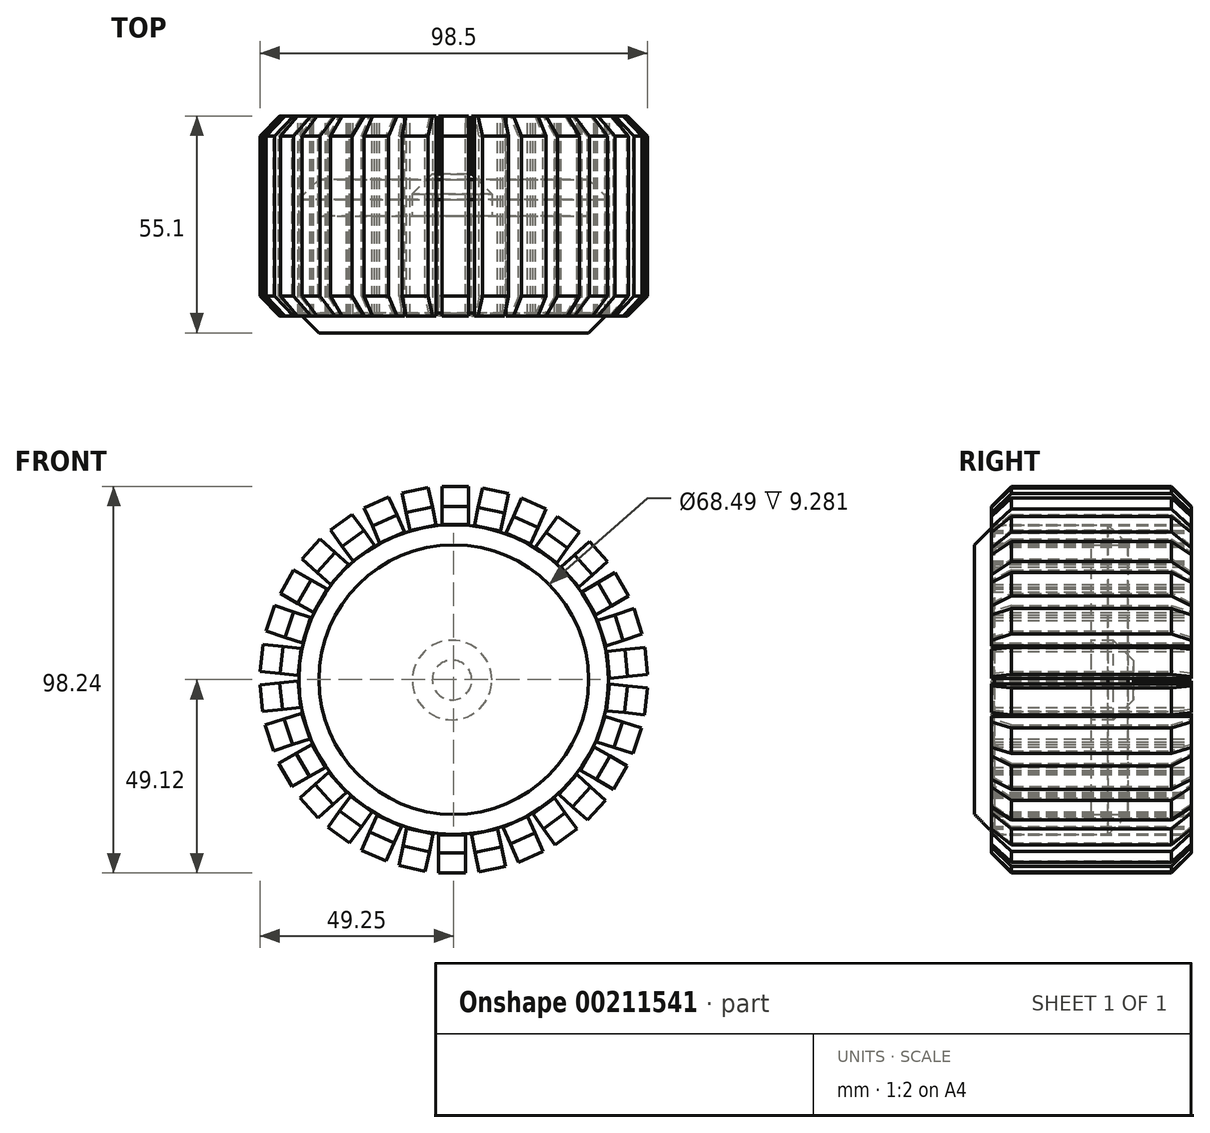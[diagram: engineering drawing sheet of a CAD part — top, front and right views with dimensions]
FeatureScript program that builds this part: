
annotation { "Feature Type Name" : "Feature", "Feature Type Description" : "" }
export const myFeature = defineFeature(function(context is Context, id is Id, definition is map)
    precondition{}
    {
        {
            var Q0;
            Q0=qCreatedBy(makeId("Front.planeOp"),FACE);
            var sketch = newSketch(context, id + "F0", { "sketchPlane" : qUnion([Q0])});
            skCircle(sketch, "E0", {"center": v(0, 0) * mm, "radius": 39.32 * mm});
            skSolve(sketch);
        }
        {
            var Q0;
            Q0 = qSketchRegion(id + "F0", true);
            extrude(context, id + "F1", {"entities" : qUnion([Q0]), "depth" : 38.98 * mm});
        }
        {
            var Q0;
            Q0=makeQuery(id+"F1.opExtrude","SWEPT_FACE",FACE,{"disambiguationData":[OSD([sQuery(id+"F0.wireOp",EDGE,"E0")])]});
            chamfer(context, id + "F9", {"entities" : qUnion([Q0]), "width" : 5.08 * mm, "tangentPropagation" : true});
        }
        {
            var Q0;
            Q0=makeQuery(id+"F1.opExtrude","CAP_FACE",FACE,{"disambiguationData":[OSD([sQuery(id+"F0.wireOp",EDGE,"E0")])],"isStart":false});
            var sketch = newSketch(context, id + "F10", { "sketchPlane" : qUnion([Q0])});
            skCircle(sketch, "E1", {"center": v(-0.43, -0.11) * mm, "radius": 10.1 * mm});
            skSolve(sketch);
        }
        {
            var Q0;
            Q0=makeQuery(id+"F10.imprint","IMPRINT",FACE,{"disambiguationData":[TD([[makeQuery(id+"F10.imprint","IMPRINT",EDGE,{"derivedFrom":sQuery(id+"F10.wireOp",EDGE,"E1")}),1.0]])]});
            extrude(context, id + "F2", {"entities" : qUnion([Q0]), "operationType" : NewBodyOperationType.ADD, "oppositeDirection" : true, "depth" : 40.36 * mm});
        }
        {
            var Q0;
            Q0=makeQuery(id+"F1.opExtrude","CAP_FACE",FACE,{"disambiguationData":[OSD([sQuery(id+"F0.wireOp",EDGE,"E0")])],"isStart":true});
            extrude(context, id + "F3", {"entities" : qUnion([Q0]), "operationType" : NewBodyOperationType.REMOVE, "oppositeDirection" : true, "depth" : 9.28 * mm});
        }
        {
            var Q0;
            Q0=makeQuery(id+"F2.opExtrude","CAP_EDGE",EDGE,{"disambiguationData":[OSD([sQuery(id+"F10.wireOp",EDGE,"E1")])],"isStart":false});
            chamfer(context, id + "F4", {"entities" : qUnion([Q0]), "width" : 5.08 * mm, "tangentPropagation" : true});
        }
        {
            var Q0;
            Q0=makeQuery(id+"F3.boolean.opBoolean","COPY",FACE,{"derivedFrom":makeQuery(id+"F3.opExtrude","CAP_FACE",FACE,{"disambiguationData":[OSD([sQuery(id+"F0.wireOp",EDGE,"E0")])],"isStart":false})});
            cPlane(context, id + "F5", {"entities" : qUnion([Q0]), "cplaneType" : CPlaneType.OFFSET, "offset" : 25.4 * mm, "width" : 152.4 * mm, "height" : 152.4 * mm});
        }
        {
            var Q0;
            Q0=qCreatedBy(id+"F5.planeOp",FACE);
            var sketch = newSketch(context, id + "F6", { "sketchPlane" : qUnion([Q0])});
            skLineSegment(sketch, "E2.bottom", {"start": v(3.02, 39.41) * mm, "end": v(-3.8, 39.41) * mm});
            skLineSegment(sketch, "E2.top", {"start": v(3.02, 49.12) * mm, "end": v(-3.8, 49.12) * mm});
            skLineSegment(sketch, "E2.left", {"start": v(3.02, 39.41) * mm, "end": v(3.02, 49.12) * mm});
            skLineSegment(sketch, "E2.right", {"start": v(-3.8, 39.41) * mm, "end": v(-3.8, 49.12) * mm});
            skPoint(sketch, "E2.middle", {"position": v(-0.4, 44.27) * mm});
            skSolve(sketch);
        }
        {
            var Q0;
            Q0 = qSketchRegion(id + "F6", true);
            extrude(context, id + "F11", {"entities" : qUnion([Q0]), "oppositeDirection" : true, "depth" : 50.8 * mm});
        }
        {
            var Q0;
            Q0=makeQuery(id+"F11.opExtrude","SWEPT_BODY",BODY,{"disambiguationData":[OSD([sQuery(id+"F6.wireOp",EDGE,"E2.bottom"),sQuery(id+"F6.wireOp",EDGE,"E2.top"),sQuery(id+"F6.wireOp",EDGE,"E2.left"),sQuery(id+"F6.wireOp",EDGE,"E2.right")])]});
            var Q1;
            Q1=makeQuery(id+"F1.opExtrude","SWEPT_FACE",FACE,{"disambiguationData":[OSD([sQuery(id+"F0.wireOp",EDGE,"E0")])]});
            circularPattern(context, id + "F7", {"operationType" : NewBodyOperationType.ADD, "entities" : qUnion([Q0]), "axis" : qUnion([Q1]), "angle" : 360 * degree, "instanceCount" : 30, "equalSpace" : true});
        }
        {
            var Q0;
            Q0=makeQuery(id+"F7.opPattern","COPY",EDGE,{"derivedFrom":makeQuery(id+"F11.opExtrude","CAP_EDGE",EDGE,{"disambiguationData":[OSD([sQuery(id+"F6.wireOp",EDGE,"E2.top")])],"isStart":false}),"instanceName":"29"});
            var Q1;
            Q1=makeQuery(id+"F11.opExtrude","CAP_EDGE",EDGE,{"disambiguationData":[OSD([sQuery(id+"F6.wireOp",EDGE,"E2.top")])],"isStart":false});
            var Q2;
            Q2=makeQuery(id+"F7.opPattern","COPY",EDGE,{"derivedFrom":makeQuery(id+"F11.opExtrude","CAP_EDGE",EDGE,{"disambiguationData":[OSD([sQuery(id+"F6.wireOp",EDGE,"E2.top")])],"isStart":false}),"instanceName":"1"});
            var Q3;
            Q3=makeQuery(id+"F7.opPattern","COPY",EDGE,{"derivedFrom":makeQuery(id+"F11.opExtrude","CAP_EDGE",EDGE,{"disambiguationData":[OSD([sQuery(id+"F6.wireOp",EDGE,"E2.top")])],"isStart":false}),"instanceName":"2"});
            var Q4;
            Q4=makeQuery(id+"F7.opPattern","COPY",EDGE,{"derivedFrom":makeQuery(id+"F11.opExtrude","CAP_EDGE",EDGE,{"disambiguationData":[OSD([sQuery(id+"F6.wireOp",EDGE,"E2.top")])],"isStart":false}),"instanceName":"3"});
            var Q5;
            Q5=makeQuery(id+"F7.opPattern","COPY",EDGE,{"derivedFrom":makeQuery(id+"F11.opExtrude","CAP_EDGE",EDGE,{"disambiguationData":[OSD([sQuery(id+"F6.wireOp",EDGE,"E2.top")])],"isStart":false}),"instanceName":"4"});
            var Q6;
            Q6=makeQuery(id+"F7.opPattern","COPY",EDGE,{"derivedFrom":makeQuery(id+"F11.opExtrude","CAP_EDGE",EDGE,{"disambiguationData":[OSD([sQuery(id+"F6.wireOp",EDGE,"E2.top")])],"isStart":false}),"instanceName":"5"});
            var Q7;
            Q7=makeQuery(id+"F7.opPattern","COPY",EDGE,{"derivedFrom":makeQuery(id+"F11.opExtrude","CAP_EDGE",EDGE,{"disambiguationData":[OSD([sQuery(id+"F6.wireOp",EDGE,"E2.top")])],"isStart":false}),"instanceName":"6"});
            var Q8;
            Q8=makeQuery(id+"F7.opPattern","COPY",EDGE,{"derivedFrom":makeQuery(id+"F11.opExtrude","CAP_EDGE",EDGE,{"disambiguationData":[OSD([sQuery(id+"F6.wireOp",EDGE,"E2.top")])],"isStart":false}),"instanceName":"7"});
            var Q9;
            Q9=makeQuery(id+"F7.opPattern","COPY",EDGE,{"derivedFrom":makeQuery(id+"F11.opExtrude","CAP_EDGE",EDGE,{"disambiguationData":[OSD([sQuery(id+"F6.wireOp",EDGE,"E2.top")])],"isStart":false}),"instanceName":"8"});
            var Q10;
            Q10=makeQuery(id+"F7.opPattern","COPY",EDGE,{"derivedFrom":makeQuery(id+"F11.opExtrude","CAP_EDGE",EDGE,{"disambiguationData":[OSD([sQuery(id+"F6.wireOp",EDGE,"E2.top")])],"isStart":false}),"instanceName":"9"});
            var Q11;
            Q11=makeQuery(id+"F7.opPattern","COPY",EDGE,{"derivedFrom":makeQuery(id+"F11.opExtrude","CAP_EDGE",EDGE,{"disambiguationData":[OSD([sQuery(id+"F6.wireOp",EDGE,"E2.top")])],"isStart":false}),"instanceName":"10"});
            var Q12;
            Q12=makeQuery(id+"F7.opPattern","COPY",EDGE,{"derivedFrom":makeQuery(id+"F11.opExtrude","CAP_EDGE",EDGE,{"disambiguationData":[OSD([sQuery(id+"F6.wireOp",EDGE,"E2.top")])],"isStart":false}),"instanceName":"11"});
            var Q13;
            Q13=makeQuery(id+"F7.opPattern","COPY",EDGE,{"derivedFrom":makeQuery(id+"F11.opExtrude","CAP_EDGE",EDGE,{"disambiguationData":[OSD([sQuery(id+"F6.wireOp",EDGE,"E2.top")])],"isStart":false}),"instanceName":"12"});
            var Q14;
            Q14=makeQuery(id+"F7.opPattern","COPY",EDGE,{"derivedFrom":makeQuery(id+"F11.opExtrude","CAP_EDGE",EDGE,{"disambiguationData":[OSD([sQuery(id+"F6.wireOp",EDGE,"E2.top")])],"isStart":false}),"instanceName":"13"});
            var Q15;
            Q15=makeQuery(id+"F7.opPattern","COPY",EDGE,{"derivedFrom":makeQuery(id+"F11.opExtrude","CAP_EDGE",EDGE,{"disambiguationData":[OSD([sQuery(id+"F6.wireOp",EDGE,"E2.top")])],"isStart":false}),"instanceName":"14"});
            var Q16;
            Q16=makeQuery(id+"F7.opPattern","COPY",EDGE,{"derivedFrom":makeQuery(id+"F11.opExtrude","CAP_EDGE",EDGE,{"disambiguationData":[OSD([sQuery(id+"F6.wireOp",EDGE,"E2.top")])],"isStart":false}),"instanceName":"15"});
            var Q17;
            Q17=makeQuery(id+"F7.opPattern","COPY",EDGE,{"derivedFrom":makeQuery(id+"F11.opExtrude","CAP_EDGE",EDGE,{"disambiguationData":[OSD([sQuery(id+"F6.wireOp",EDGE,"E2.top")])],"isStart":false}),"instanceName":"16"});
            var Q18;
            Q18=makeQuery(id+"F7.opPattern","COPY",EDGE,{"derivedFrom":makeQuery(id+"F11.opExtrude","CAP_EDGE",EDGE,{"disambiguationData":[OSD([sQuery(id+"F6.wireOp",EDGE,"E2.top")])],"isStart":false}),"instanceName":"17"});
            var Q19;
            Q19=makeQuery(id+"F7.opPattern","COPY",EDGE,{"derivedFrom":makeQuery(id+"F11.opExtrude","CAP_EDGE",EDGE,{"disambiguationData":[OSD([sQuery(id+"F6.wireOp",EDGE,"E2.top")])],"isStart":false}),"instanceName":"18"});
            var Q20;
            Q20=makeQuery(id+"F7.opPattern","COPY",EDGE,{"derivedFrom":makeQuery(id+"F11.opExtrude","CAP_EDGE",EDGE,{"disambiguationData":[OSD([sQuery(id+"F6.wireOp",EDGE,"E2.top")])],"isStart":false}),"instanceName":"19"});
            var Q21;
            Q21=makeQuery(id+"F7.opPattern","COPY",EDGE,{"derivedFrom":makeQuery(id+"F11.opExtrude","CAP_EDGE",EDGE,{"disambiguationData":[OSD([sQuery(id+"F6.wireOp",EDGE,"E2.top")])],"isStart":false}),"instanceName":"20"});
            var Q22;
            Q22=makeQuery(id+"F7.opPattern","COPY",EDGE,{"derivedFrom":makeQuery(id+"F11.opExtrude","CAP_EDGE",EDGE,{"disambiguationData":[OSD([sQuery(id+"F6.wireOp",EDGE,"E2.top")])],"isStart":false}),"instanceName":"21"});
            var Q23;
            Q23=makeQuery(id+"F7.opPattern","COPY",EDGE,{"derivedFrom":makeQuery(id+"F11.opExtrude","CAP_EDGE",EDGE,{"disambiguationData":[OSD([sQuery(id+"F6.wireOp",EDGE,"E2.top")])],"isStart":false}),"instanceName":"22"});
            var Q24;
            Q24=makeQuery(id+"F7.opPattern","COPY",EDGE,{"derivedFrom":makeQuery(id+"F11.opExtrude","CAP_EDGE",EDGE,{"disambiguationData":[OSD([sQuery(id+"F6.wireOp",EDGE,"E2.top")])],"isStart":false}),"instanceName":"23"});
            var Q25;
            Q25=makeQuery(id+"F7.opPattern","COPY",EDGE,{"derivedFrom":makeQuery(id+"F11.opExtrude","CAP_EDGE",EDGE,{"disambiguationData":[OSD([sQuery(id+"F6.wireOp",EDGE,"E2.top")])],"isStart":false}),"instanceName":"24"});
            var Q26;
            Q26=makeQuery(id+"F7.opPattern","COPY",EDGE,{"derivedFrom":makeQuery(id+"F11.opExtrude","CAP_EDGE",EDGE,{"disambiguationData":[OSD([sQuery(id+"F6.wireOp",EDGE,"E2.top")])],"isStart":false}),"instanceName":"25"});
            var Q27;
            Q27=makeQuery(id+"F7.opPattern","COPY",EDGE,{"derivedFrom":makeQuery(id+"F11.opExtrude","CAP_EDGE",EDGE,{"disambiguationData":[OSD([sQuery(id+"F6.wireOp",EDGE,"E2.top")])],"isStart":false}),"instanceName":"26"});
            var Q28;
            Q28=makeQuery(id+"F7.opPattern","COPY",EDGE,{"derivedFrom":makeQuery(id+"F11.opExtrude","CAP_EDGE",EDGE,{"disambiguationData":[OSD([sQuery(id+"F6.wireOp",EDGE,"E2.top")])],"isStart":false}),"instanceName":"27"});
            var Q29;
            Q29=makeQuery(id+"F7.opPattern","COPY",EDGE,{"derivedFrom":makeQuery(id+"F11.opExtrude","CAP_EDGE",EDGE,{"disambiguationData":[OSD([sQuery(id+"F6.wireOp",EDGE,"E2.top")])],"isStart":false}),"instanceName":"28"});
            chamfer(context, id + "F12", {"entities" : qUnion([Q0, Q1, Q2, Q3, Q4, Q5, Q6, Q7, Q8, Q9, Q10, Q11, Q12, Q13, Q14, Q15, Q16, Q17, Q18, Q19, Q20, Q21, Q22, Q23, Q24, Q25, Q26, Q27, Q28, Q29]), "width" : 5.08 * mm, "tangentPropagation" : true});
        }
        {
            var Q0;
            Q0=makeQuery(id+"F7.opPattern","COPY",EDGE,{"derivedFrom":makeQuery(id+"F11.opExtrude","CAP_EDGE",EDGE,{"disambiguationData":[OSD([sQuery(id+"F6.wireOp",EDGE,"E2.top")])],"isStart":true}),"instanceName":"28"});
            var Q1;
            Q1=makeQuery(id+"F7.opPattern","COPY",EDGE,{"derivedFrom":makeQuery(id+"F11.opExtrude","CAP_EDGE",EDGE,{"disambiguationData":[OSD([sQuery(id+"F6.wireOp",EDGE,"E2.top")])],"isStart":true}),"instanceName":"27"});
            var Q2;
            Q2=makeQuery(id+"F7.opPattern","COPY",EDGE,{"derivedFrom":makeQuery(id+"F11.opExtrude","CAP_EDGE",EDGE,{"disambiguationData":[OSD([sQuery(id+"F6.wireOp",EDGE,"E2.top")])],"isStart":true}),"instanceName":"29"});
            var Q3;
            Q3=makeQuery(id+"F11.opExtrude","CAP_EDGE",EDGE,{"disambiguationData":[OSD([sQuery(id+"F6.wireOp",EDGE,"E2.top")])],"isStart":true});
            var Q4;
            Q4=makeQuery(id+"F7.opPattern","COPY",EDGE,{"derivedFrom":makeQuery(id+"F11.opExtrude","CAP_EDGE",EDGE,{"disambiguationData":[OSD([sQuery(id+"F6.wireOp",EDGE,"E2.top")])],"isStart":true}),"instanceName":"1"});
            var Q5;
            Q5=makeQuery(id+"F7.opPattern","COPY",EDGE,{"derivedFrom":makeQuery(id+"F11.opExtrude","CAP_EDGE",EDGE,{"disambiguationData":[OSD([sQuery(id+"F6.wireOp",EDGE,"E2.top")])],"isStart":true}),"instanceName":"2"});
            var Q6;
            Q6=makeQuery(id+"F7.opPattern","COPY",EDGE,{"derivedFrom":makeQuery(id+"F11.opExtrude","CAP_EDGE",EDGE,{"disambiguationData":[OSD([sQuery(id+"F6.wireOp",EDGE,"E2.top")])],"isStart":true}),"instanceName":"3"});
            var Q7;
            Q7=makeQuery(id+"F7.opPattern","COPY",EDGE,{"derivedFrom":makeQuery(id+"F11.opExtrude","CAP_EDGE",EDGE,{"disambiguationData":[OSD([sQuery(id+"F6.wireOp",EDGE,"E2.top")])],"isStart":true}),"instanceName":"4"});
            var Q8;
            Q8=makeQuery(id+"F7.opPattern","COPY",EDGE,{"derivedFrom":makeQuery(id+"F11.opExtrude","CAP_EDGE",EDGE,{"disambiguationData":[OSD([sQuery(id+"F6.wireOp",EDGE,"E2.top")])],"isStart":true}),"instanceName":"5"});
            var Q9;
            Q9=makeQuery(id+"F7.opPattern","COPY",EDGE,{"derivedFrom":makeQuery(id+"F11.opExtrude","CAP_EDGE",EDGE,{"disambiguationData":[OSD([sQuery(id+"F6.wireOp",EDGE,"E2.top")])],"isStart":true}),"instanceName":"6"});
            var Q10;
            Q10=makeQuery(id+"F7.opPattern","COPY",EDGE,{"derivedFrom":makeQuery(id+"F11.opExtrude","CAP_EDGE",EDGE,{"disambiguationData":[OSD([sQuery(id+"F6.wireOp",EDGE,"E2.top")])],"isStart":true}),"instanceName":"7"});
            var Q11;
            Q11=makeQuery(id+"F7.opPattern","COPY",EDGE,{"derivedFrom":makeQuery(id+"F11.opExtrude","CAP_EDGE",EDGE,{"disambiguationData":[OSD([sQuery(id+"F6.wireOp",EDGE,"E2.top")])],"isStart":true}),"instanceName":"8"});
            var Q12;
            Q12=makeQuery(id+"F7.opPattern","COPY",EDGE,{"derivedFrom":makeQuery(id+"F11.opExtrude","CAP_EDGE",EDGE,{"disambiguationData":[OSD([sQuery(id+"F6.wireOp",EDGE,"E2.top")])],"isStart":true}),"instanceName":"9"});
            var Q13;
            Q13=makeQuery(id+"F7.opPattern","COPY",EDGE,{"derivedFrom":makeQuery(id+"F11.opExtrude","CAP_EDGE",EDGE,{"disambiguationData":[OSD([sQuery(id+"F6.wireOp",EDGE,"E2.top")])],"isStart":true}),"instanceName":"10"});
            var Q14;
            Q14=makeQuery(id+"F7.opPattern","COPY",EDGE,{"derivedFrom":makeQuery(id+"F11.opExtrude","CAP_EDGE",EDGE,{"disambiguationData":[OSD([sQuery(id+"F6.wireOp",EDGE,"E2.top")])],"isStart":true}),"instanceName":"11"});
            var Q15;
            Q15=makeQuery(id+"F7.opPattern","COPY",EDGE,{"derivedFrom":makeQuery(id+"F11.opExtrude","CAP_EDGE",EDGE,{"disambiguationData":[OSD([sQuery(id+"F6.wireOp",EDGE,"E2.top")])],"isStart":true}),"instanceName":"12"});
            var Q16;
            Q16=makeQuery(id+"F7.opPattern","COPY",EDGE,{"derivedFrom":makeQuery(id+"F11.opExtrude","CAP_EDGE",EDGE,{"disambiguationData":[OSD([sQuery(id+"F6.wireOp",EDGE,"E2.top")])],"isStart":true}),"instanceName":"13"});
            var Q17;
            Q17=makeQuery(id+"F7.opPattern","COPY",EDGE,{"derivedFrom":makeQuery(id+"F11.opExtrude","CAP_EDGE",EDGE,{"disambiguationData":[OSD([sQuery(id+"F6.wireOp",EDGE,"E2.top")])],"isStart":true}),"instanceName":"14"});
            var Q18;
            Q18=makeQuery(id+"F7.opPattern","COPY",EDGE,{"derivedFrom":makeQuery(id+"F11.opExtrude","CAP_EDGE",EDGE,{"disambiguationData":[OSD([sQuery(id+"F6.wireOp",EDGE,"E2.top")])],"isStart":true}),"instanceName":"15"});
            var Q19;
            Q19=makeQuery(id+"F7.opPattern","COPY",EDGE,{"derivedFrom":makeQuery(id+"F11.opExtrude","CAP_EDGE",EDGE,{"disambiguationData":[OSD([sQuery(id+"F6.wireOp",EDGE,"E2.top")])],"isStart":true}),"instanceName":"16"});
            var Q20;
            Q20=makeQuery(id+"F7.opPattern","COPY",EDGE,{"derivedFrom":makeQuery(id+"F11.opExtrude","CAP_EDGE",EDGE,{"disambiguationData":[OSD([sQuery(id+"F6.wireOp",EDGE,"E2.top")])],"isStart":true}),"instanceName":"17"});
            var Q21;
            Q21=makeQuery(id+"F7.opPattern","COPY",EDGE,{"derivedFrom":makeQuery(id+"F11.opExtrude","CAP_EDGE",EDGE,{"disambiguationData":[OSD([sQuery(id+"F6.wireOp",EDGE,"E2.top")])],"isStart":true}),"instanceName":"18"});
            var Q22;
            Q22=makeQuery(id+"F7.opPattern","COPY",EDGE,{"derivedFrom":makeQuery(id+"F11.opExtrude","CAP_EDGE",EDGE,{"disambiguationData":[OSD([sQuery(id+"F6.wireOp",EDGE,"E2.top")])],"isStart":true}),"instanceName":"19"});
            var Q23;
            Q23=makeQuery(id+"F7.opPattern","COPY",EDGE,{"derivedFrom":makeQuery(id+"F11.opExtrude","CAP_EDGE",EDGE,{"disambiguationData":[OSD([sQuery(id+"F6.wireOp",EDGE,"E2.top")])],"isStart":true}),"instanceName":"20"});
            var Q24;
            Q24=makeQuery(id+"F7.opPattern","COPY",EDGE,{"derivedFrom":makeQuery(id+"F11.opExtrude","CAP_EDGE",EDGE,{"disambiguationData":[OSD([sQuery(id+"F6.wireOp",EDGE,"E2.top")])],"isStart":true}),"instanceName":"21"});
            var Q25;
            Q25=makeQuery(id+"F7.opPattern","COPY",EDGE,{"derivedFrom":makeQuery(id+"F11.opExtrude","CAP_EDGE",EDGE,{"disambiguationData":[OSD([sQuery(id+"F6.wireOp",EDGE,"E2.top")])],"isStart":true}),"instanceName":"22"});
            var Q26;
            Q26=makeQuery(id+"F7.opPattern","COPY",EDGE,{"derivedFrom":makeQuery(id+"F11.opExtrude","CAP_EDGE",EDGE,{"disambiguationData":[OSD([sQuery(id+"F6.wireOp",EDGE,"E2.top")])],"isStart":true}),"instanceName":"23"});
            var Q27;
            Q27=makeQuery(id+"F7.opPattern","COPY",EDGE,{"derivedFrom":makeQuery(id+"F11.opExtrude","CAP_EDGE",EDGE,{"disambiguationData":[OSD([sQuery(id+"F6.wireOp",EDGE,"E2.top")])],"isStart":true}),"instanceName":"24"});
            var Q28;
            Q28=makeQuery(id+"F7.opPattern","COPY",EDGE,{"derivedFrom":makeQuery(id+"F11.opExtrude","CAP_EDGE",EDGE,{"disambiguationData":[OSD([sQuery(id+"F6.wireOp",EDGE,"E2.top")])],"isStart":true}),"instanceName":"25"});
            var Q29;
            Q29=makeQuery(id+"F7.opPattern","COPY",EDGE,{"derivedFrom":makeQuery(id+"F11.opExtrude","CAP_EDGE",EDGE,{"disambiguationData":[OSD([sQuery(id+"F6.wireOp",EDGE,"E2.top")])],"isStart":true}),"instanceName":"26"});
            chamfer(context, id + "F8", {"entities" : qUnion([Q0, Q1, Q2, Q3, Q4, Q5, Q6, Q7, Q8, Q9, Q10, Q11, Q12, Q13, Q14, Q15, Q16, Q17, Q18, Q19, Q20, Q21, Q22, Q23, Q24, Q25, Q26, Q27, Q28, Q29]), "width" : 5.08 * mm, "tangentPropagation" : true});
        }
    });
